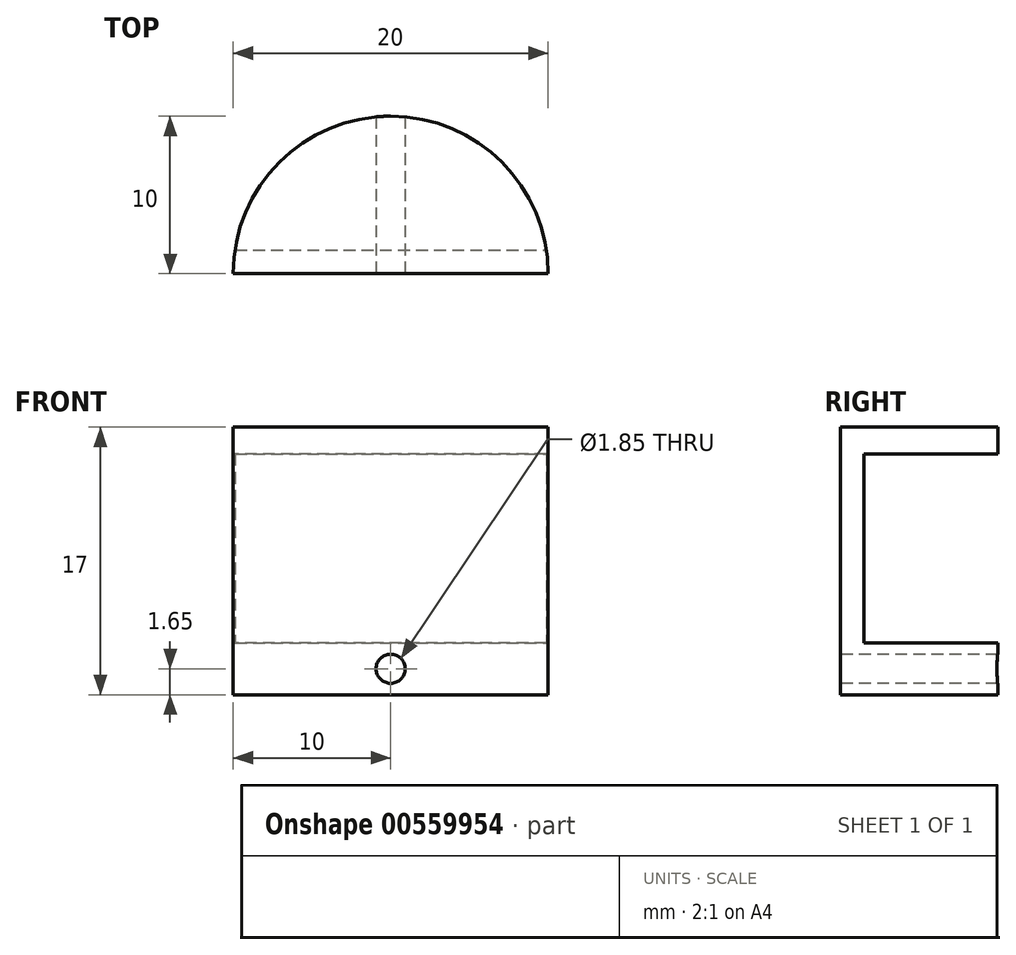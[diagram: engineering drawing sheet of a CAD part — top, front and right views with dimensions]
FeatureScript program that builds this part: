
annotation { "Feature Type Name" : "Feature", "Feature Type Description" : "" }
export const myFeature = defineFeature(function(context is Context, id is Id, definition is map)
    precondition{}
    {
        {
            var Q0;
            Q0=qCreatedBy(makeId("Top.planeOp"),FACE);
            var sketch = newSketch(context, id + "F0", { "sketchPlane" : qUnion([Q0])});
            skArc(sketch, "E0", {"start": v(10, 0) * mm, "mid": v(0, 10) * mm, "end": v(-10, 0) * mm});
            skLineSegment(sketch, "E1", {"start": v(-10, 0) * mm, "end": v(10, 0) * mm});
            skSolve(sketch);
        }
        {
            var Q0;
            Q0=makeQuery(id+"F0.imprint","IMPRINT",FACE,{"disambiguationData":[TD([[makeQuery(id+"F0.imprint","IMPRINT",EDGE,{"derivedFrom":sQuery(id+"F0.wireOp",EDGE,"E0")}),1.0]])]});
            extrude(context, id + "F1", {"entities" : qUnion([Q0]), "depth" : 17 * mm, "offsetDistance" : 25 * mm});
        }
        {
            var Q0;
            Q0=qCreatedBy(makeId("Top.planeOp"),FACE);
            cPlane(context, id + "F2", {"entities" : qUnion([Q0]), "cplaneType" : CPlaneType.OFFSET, "offset" : 3.3 * mm, "width" : 150 * mm, "height" : 150 * mm});
        }
        {
            var Q0;
            Q0=qCreatedBy(id+"F2.planeOp",FACE);
            var sketch = newSketch(context, id + "F3", { "sketchPlane" : qUnion([Q0])});
            skLineSegment(sketch, "E2.bottom", {"start": v(-11.41, 13.5) * mm, "end": v(10.59, 13.5) * mm});
            skLineSegment(sketch, "E2.top", {"start": v(-11.41, 1.5) * mm, "end": v(10.59, 1.5) * mm});
            skLineSegment(sketch, "E2.left", {"start": v(-11.41, 13.5) * mm, "end": v(-11.41, 1.5) * mm});
            skLineSegment(sketch, "E2.right", {"start": v(10.59, 13.5) * mm, "end": v(10.59, 1.5) * mm});
            skSolve(sketch);
        }
        {
            var Q0;
            Q0 = qSketchRegion(id + "F3", true);
            extrude(context, id + "F4", {"entities" : qUnion([Q0]), "operationType" : NewBodyOperationType.REMOVE, "oppositeDirection" : true, "depth" : -12 * mm, "offsetDistance" : 25 * mm});
        }
        {
            var Q0;
            Q0=qCreatedBy(makeId("Front.planeOp"),FACE);
            var sketch = newSketch(context, id + "F5", { "sketchPlane" : qUnion([Q0])});
            skCircle(sketch, "E3", {"center": v(0, 1.65) * mm, "radius": 0.93 * mm});
            skLineSegment(sketch, "E4", {"start": v(0, 0) * mm, "end": v(0, 3.3) * mm, "construction": true});
            skSolve(sketch);
        }
        {
            var Q0;
            Q0 = qSketchRegion(id + "F5", true);
            extrude(context, id + "F6", {"entities" : qUnion([Q0]), "operationType" : NewBodyOperationType.REMOVE, "oppositeDirection" : true, "depth" : 12 * mm, "offsetDistance" : 25 * mm});
        }
    });
